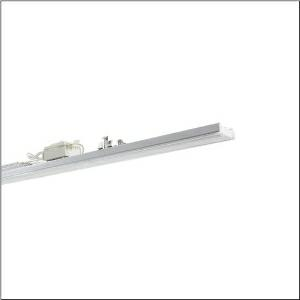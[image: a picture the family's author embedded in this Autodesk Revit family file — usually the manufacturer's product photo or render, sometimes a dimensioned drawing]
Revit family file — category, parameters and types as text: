
# Revit family: licross_r__11_recessed_mo_51tl107n485g_ff75
name_source: partatom
category: Lighting Fixtures
units: mm (PartAtom-declared; Revit-internal decimal feet)

## family parameters
Cut with Voids When Loaded = No
Host = Face
Light Source = No
Part Type = Normal
Room Calculation Point = No
Round Connector Dimension = Use Diameter
Shared = No

## types (1)
- Licross® 11 Recessed MO (1 x LED, 8700 lm, 48.5 W, 4000K)
    Apparent Load = 49 VA
    CIE Flux Codes = 50 81 96 100 100
    Color Rendering = 80
    Color Temperature = 4000K
    Default Elevation = 1800 mm
    Description = Licross® 11 Recessed MO, luminaire insert, of sheet steel, coil coated, white, length: 1.500mm, width: 66mm, height: 67mm, LED rated luminous flux: 8.710lm, light colour: 840, control gear: ON/OFF, with plug, 3-pole, with phase selection, mains connection: 220..240V, AC, 50/60Hz, rated input power: 49W, halogen-free wiring, primary optical cover: cover, of PMMA, light emission: direct distribution, primary light characteristic: symmetric, protection rating (complete): IP40, insulation class (complete): insulation class I (protective earthing), certification: CE, ENEC, VDE, UKCA, protection symbol: D if used in an environment without relevant dust loads with corresponding accessories, impact resistance: IK06, permissible ambient temperature for indoor applications: -35..+35°C, corresponds to IFS (International Featured Standards) requirements for safety and quality in the food industry, reducing of maximum allowable ambient temperature of 5°C with ceiling mounting, packaging unit: 1 piece
    Height = 58 mm
    Lamp = 1 x LED
    Lamp Light Flux = 8700 lm
    Lamp Power = 48.5 W
    Lamp count = 1
    Length = 1500 mm
    Luminous efficacy = 179 lm/W
    Manufacturer = Siteco
    ModVariant = No
    Model = 51TL107N485G
    Mounting Place = Ceiling
    Mounting Type = Pendant
    Number of Poles = 1
    OnlyDefault = Yes
    Power Factor = 1
    Product Name = Licross® 11 Recessed MO
    Product group = luminaire insert
    ProductGroupID = 902
    Protection Class = Protection class I
    Protection Degree = IP 40
    RLX_Detail_Level = 1
    RLX_Emergency_Light_Flux = 0 lm
    RLX_Emergency_Type = 0
    RLX_Emergency_Type_DB = No
    RlxData = <blob elided: 20665 chars, md5=1c4ac11e>
    Socket = socket
    Standby Power = 0 W
    System Light Flux = 8700 lm
    System Power = 49 W
    Type Comments = Product without accessories
    Type Image = l_1296930.jpg
    URL = http://relux.com
    VarID = ---
    Voltage = 0 V
    Weight = 0.00 kg
    Width = 66 mm

## geometry (parser evidence)
native form markers: Blend x4, Sweep x12
no freeform markers — native parametric forms only
